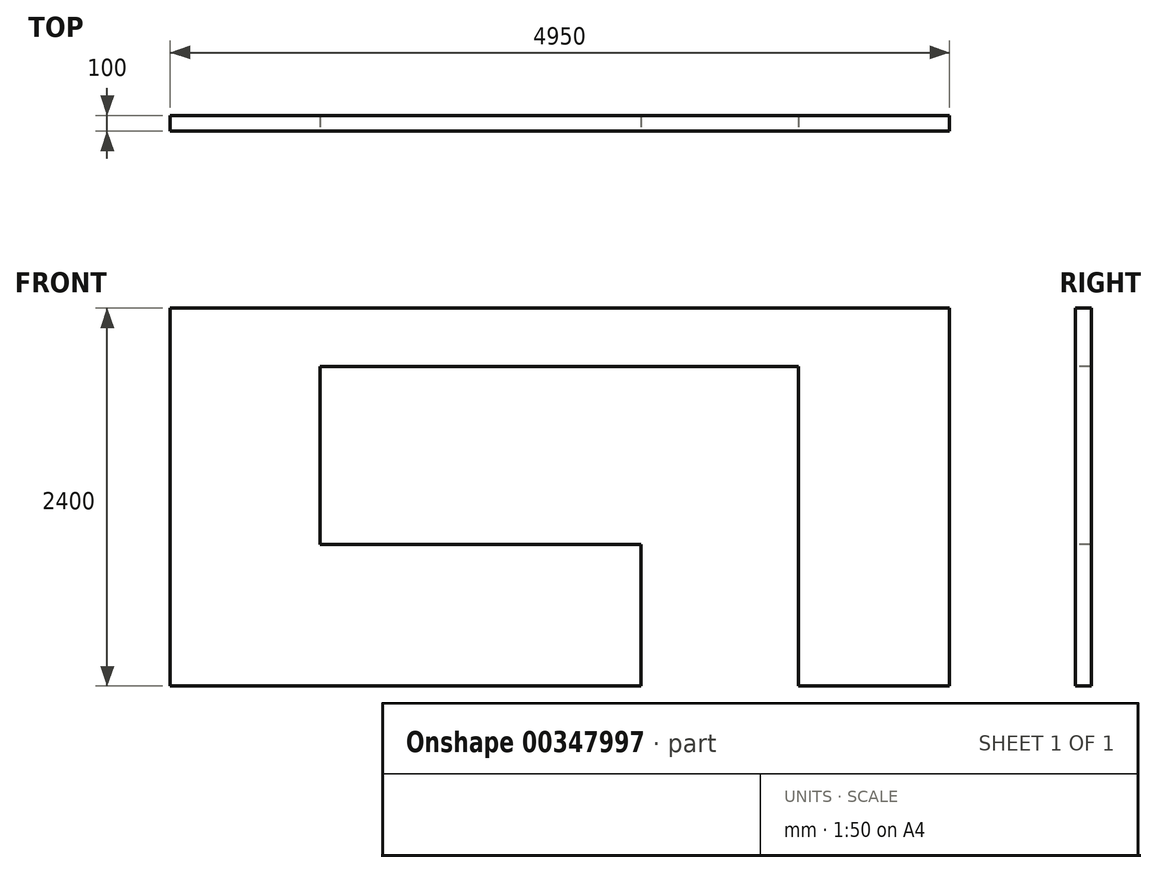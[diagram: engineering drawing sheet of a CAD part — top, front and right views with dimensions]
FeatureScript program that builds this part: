
annotation { "Feature Type Name" : "Feature", "Feature Type Description" : "" }
export const myFeature = defineFeature(function(context is Context, id is Id, definition is map)
    precondition{}
    {
        {
            var Q0;
            Q0=qCreatedBy(makeId("Front.planeOp"),FACE);
            var sketch = newSketch(context, id + "F0", { "sketchPlane" : qUnion([Q0])});
            skLineSegment(sketch, "E0.bottom", {"start": v(0, 0) * mm, "end": v(4950, 0) * mm});
            skLineSegment(sketch, "E0.top", {"start": v(0, 2400) * mm, "end": v(4950, 2400) * mm});
            skLineSegment(sketch, "E0.left", {"start": v(0, 0) * mm, "end": v(0, 2400) * mm});
            skLineSegment(sketch, "E0.right", {"start": v(4950, 0) * mm, "end": v(4950, 2400) * mm});
            skLineSegment(sketch, "E1", {"start": v(3990, 0) * mm, "end": v(3990, 2030) * mm});
            skLineSegment(sketch, "E2", {"start": v(950, 2030) * mm, "end": v(950, 900) * mm});
            skLineSegment(sketch, "E3", {"start": v(2990, 900) * mm, "end": v(2990, 0) * mm});
            skLineSegment(sketch, "E4", {"start": v(950, 900) * mm, "end": v(2990, 900) * mm});
            skLineSegment(sketch, "E5", {"start": v(950, 2030) * mm, "end": v(3990, 2030) * mm});
            skSolve(sketch);
        }
        {
            var Q0;
            Q0=makeQuery(id+"F0.imprint","IMPRINT",FACE,{"disambiguationData":[TD([[makeQuery(id+"F0.imprint","IMPRINT",EDGE,{"derivedFrom":sQuery(id+"F0.wireOp",EDGE,"E0.top")}),-1.0]])]});
            extrude(context, id + "F1", {"entities" : qUnion([Q0]), "oppositeDirection" : true, "depth" : 100 * mm});
        }
    });
